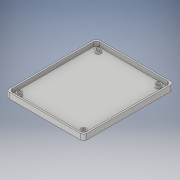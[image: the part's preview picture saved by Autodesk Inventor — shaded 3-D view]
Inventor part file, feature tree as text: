
AUTODESK INVENTOR PART (.ipt)
format: ipt  version: 2018.3 (Build 223284000, 284)  size: 160,768 bytes
history: native  units: in
note: dims shown in document units (in); Inventor stores cm internally (conversion verified against a paired STEP export)
features: extrude x3, sketch x1, fillet x1
ambient origin geometry x8: Origin, YZ Plane, XZ Plane, XY Plane, X Axis, Y Axis, Z Axis, Center Point
bodies: Solid1 (feature_tree)
feature tree (5):
  sketch  "Sketch1"  dims[d0=0.126in d1=2.25in d2=2.4in d3=2.875in d4=2.7in d5=3.175in d6=0.1in d7=0.1in d8=0.0591in d9=0.1969in d10=0.05in d11=0.0in d12=0.1in d13=0.0in d14=0.063in d15=0.0in d16=0.15in d17=0.15in d18=0.15in d19=0.125in]
  extrude  "Extrusion1"  Depth=0.125in
  extrude  "Extrusion2"  Depth=0.125in
  extrude  "Extrusion3"  Depth=0.125in
  fillet  "Fillet1"  Radius=2.7in
